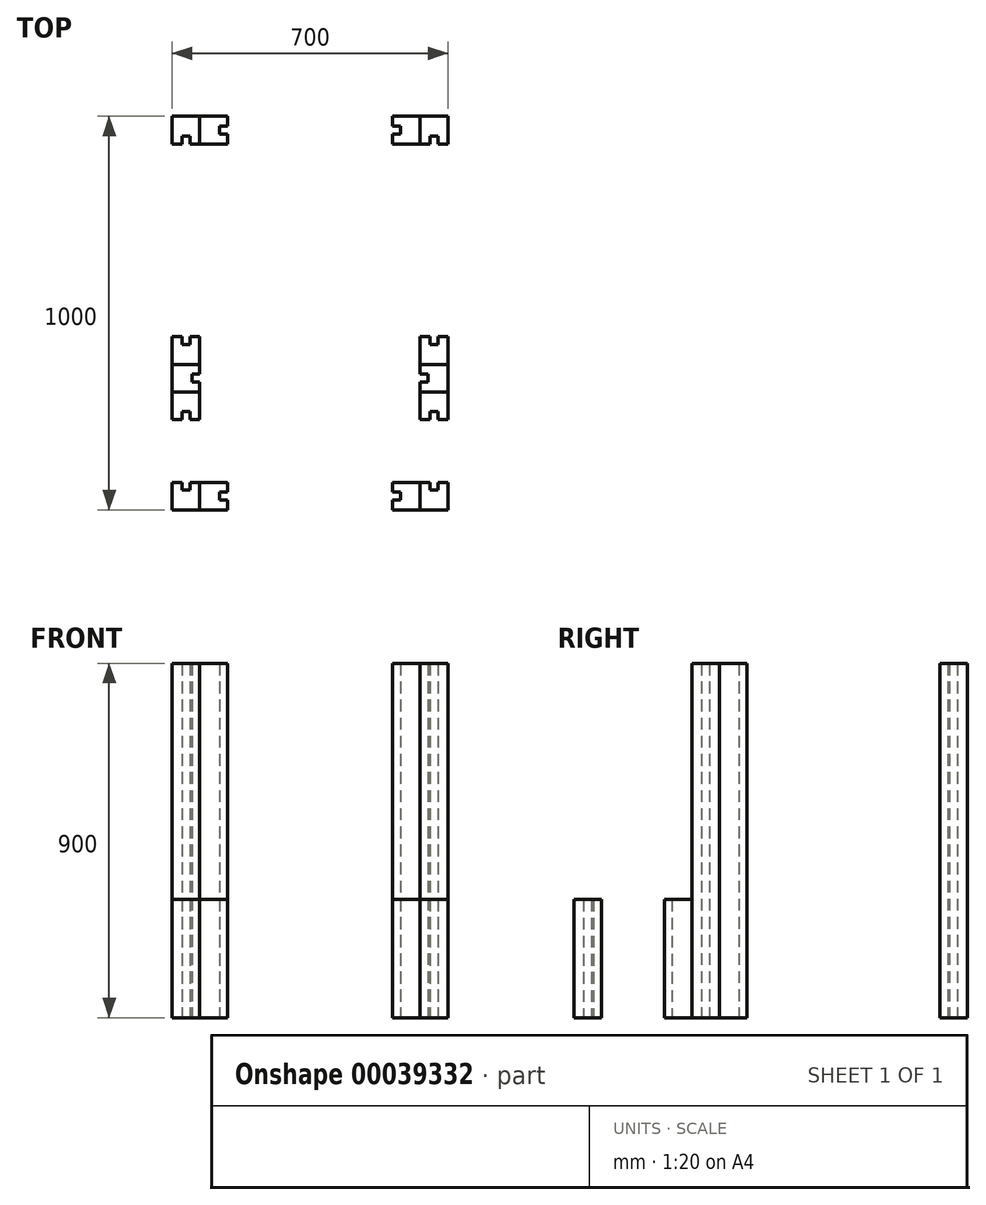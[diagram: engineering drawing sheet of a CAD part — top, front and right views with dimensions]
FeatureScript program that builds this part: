
annotation { "Feature Type Name" : "Feature", "Feature Type Description" : "" }
export const myFeature = defineFeature(function(context is Context, id is Id, definition is map)
    precondition{}
    {
        {
            var Q0;
            Q0=qCreatedBy(makeId("Top.planeOp"),FACE);
            var sketch = newSketch(context, id + "F0", { "sketchPlane" : qUnion([Q0])});
            skLineSegment(sketch, "E0", {"start": v(-350, 0) * mm, "end": v(-280, 0) * mm});
            skLineSegment(sketch, "E1", {"start": v(-280, 0) * mm, "end": v(-280, -70) * mm});
            skLineSegment(sketch, "E2", {"start": v(-280, -70) * mm, "end": v(-305, -70) * mm});
            skLineSegment(sketch, "E3", {"start": v(-305, -70) * mm, "end": v(-305, -50) * mm});
            skLineSegment(sketch, "E4", {"start": v(-305, -50) * mm, "end": v(-325, -50) * mm});
            skLineSegment(sketch, "E5", {"start": v(-325, -50) * mm, "end": v(-325, -70) * mm});
            skLineSegment(sketch, "E6", {"start": v(-325, -70) * mm, "end": v(-350, -70) * mm});
            skLineSegment(sketch, "E7", {"start": v(-350, -70) * mm, "end": v(-350, 0) * mm});
            skLineSegment(sketch, "E8", {"start": v(-350, -630) * mm, "end": v(-325, -630) * mm});
            skLineSegment(sketch, "E9", {"start": v(-325, -630) * mm, "end": v(-325, -650) * mm});
            skLineSegment(sketch, "E10", {"start": v(-325, -650) * mm, "end": v(-305, -650) * mm});
            skLineSegment(sketch, "E11", {"start": v(-305, -650) * mm, "end": v(-305, -630) * mm});
            skLineSegment(sketch, "E12", {"start": v(-305, -630) * mm, "end": v(-280, -630) * mm});
            skLineSegment(sketch, "E13", {"start": v(-280, -630) * mm, "end": v(-280, -700) * mm});
            skLineSegment(sketch, "E14", {"start": v(-280, -700) * mm, "end": v(-350, -700) * mm});
            skLineSegment(sketch, "E15", {"start": v(-350, -700) * mm, "end": v(-350, -630) * mm});
            skLineSegment(sketch, "E16", {"start": v(-350, -700) * mm, "end": v(-350, -770) * mm});
            skLineSegment(sketch, "E17", {"start": v(-350, -770) * mm, "end": v(-325, -770) * mm});
            skLineSegment(sketch, "E18", {"start": v(-325, -770) * mm, "end": v(-325, -750) * mm});
            skLineSegment(sketch, "E19", {"start": v(-325, -750) * mm, "end": v(-305, -750) * mm});
            skLineSegment(sketch, "E20", {"start": v(-305, -750) * mm, "end": v(-305, -770) * mm});
            skLineSegment(sketch, "E21", {"start": v(-305, -770) * mm, "end": v(-280, -770) * mm});
            skLineSegment(sketch, "E22", {"start": v(-280, -770) * mm, "end": v(-280, -700) * mm});
            skLineSegment(sketch, "E23", {"start": v(-350, -930) * mm, "end": v(-325, -930) * mm});
            skLineSegment(sketch, "E24", {"start": v(-325, -930) * mm, "end": v(-325, -950) * mm});
            skLineSegment(sketch, "E25", {"start": v(-325, -950) * mm, "end": v(-305, -950) * mm});
            skLineSegment(sketch, "E26", {"start": v(-305, -950) * mm, "end": v(-305, -930) * mm});
            skLineSegment(sketch, "E27", {"start": v(-305, -930) * mm, "end": v(-280, -930) * mm});
            skLineSegment(sketch, "E28", {"start": v(-280, -930) * mm, "end": v(-280, -1000) * mm});
            skLineSegment(sketch, "E29", {"start": v(-280, -1000) * mm, "end": v(-350, -1000) * mm});
            skLineSegment(sketch, "E30", {"start": v(-350, -1000) * mm, "end": v(-350, -930) * mm});
            skLineSegment(sketch, "E31", {"start": v(-280, 0) * mm, "end": v(-210, 0) * mm});
            skLineSegment(sketch, "E32", {"start": v(-210, 0) * mm, "end": v(-210, -25) * mm});
            skLineSegment(sketch, "E33", {"start": v(-210, -25) * mm, "end": v(-230, -25) * mm});
            skLineSegment(sketch, "E34", {"start": v(-230, -25) * mm, "end": v(-230, -45) * mm});
            skLineSegment(sketch, "E35", {"start": v(-230, -45) * mm, "end": v(-210, -45) * mm});
            skLineSegment(sketch, "E36", {"start": v(-210, -45) * mm, "end": v(-210, -70) * mm});
            skLineSegment(sketch, "E37", {"start": v(-210, -70) * mm, "end": v(-280, -70) * mm});
            skLineSegment(sketch, "E38", {"start": v(-280, -630) * mm, "end": v(-210, -630) * mm});
            skLineSegment(sketch, "E39", {"start": v(-210, -630) * mm, "end": v(-210, -655) * mm});
            skLineSegment(sketch, "E40", {"start": v(-210, -655) * mm, "end": v(-230, -655) * mm});
            skLineSegment(sketch, "E41", {"start": v(-230, -655) * mm, "end": v(-230, -675) * mm});
            skLineSegment(sketch, "E42", {"start": v(-230, -675) * mm, "end": v(-210, -675) * mm});
            skLineSegment(sketch, "E43", {"start": v(-210, -675) * mm, "end": v(-210, -700) * mm});
            skLineSegment(sketch, "E44", {"start": v(-210, -700) * mm, "end": v(-280, -700) * mm});
            skLineSegment(sketch, "E45", {"start": v(-280, -930) * mm, "end": v(-210, -930) * mm});
            skLineSegment(sketch, "E46", {"start": v(-210, -930) * mm, "end": v(-210, -955) * mm});
            skLineSegment(sketch, "E47", {"start": v(-210, -955) * mm, "end": v(-230, -955) * mm});
            skLineSegment(sketch, "E48", {"start": v(-230, -955) * mm, "end": v(-230, -975) * mm});
            skLineSegment(sketch, "E49", {"start": v(-230, -975) * mm, "end": v(-210, -975) * mm});
            skLineSegment(sketch, "E50", {"start": v(-210, -975) * mm, "end": v(-210, -1000) * mm});
            skLineSegment(sketch, "E51", {"start": v(-210, -1000) * mm, "end": v(-280, -1000) * mm});
            skSolve(sketch);
        }
        {
            var Q0;
            Q0=makeQuery(id+"F0.imprint","IMPRINT",FACE,{"disambiguationData":[TD([[makeQuery(id+"F0.imprint","IMPRINT",EDGE,{"derivedFrom":sQuery(id+"F0.wireOp",EDGE,"E0")}),-1.0]])]});
            extrude(context, id + "F1", {"entities" : qUnion([Q0]), "depth" : 900 * mm});
        }
        {
            var Q0;
            Q0=makeQuery(id+"F0.imprint","IMPRINT",FACE,{"disambiguationData":[TD([[makeQuery(id+"F0.imprint","IMPRINT",EDGE,{"derivedFrom":sQuery(id+"F0.wireOp",EDGE,"E1")}),1.0]])]});
            var Q1;
            Q1=makeQuery(id+"F1.opExtrude","CAP_FACE",FACE,{"disambiguationData":[OSD([sQuery(id+"F0.wireOp",EDGE,"E0"),sQuery(id+"F0.wireOp",EDGE,"E1"),sQuery(id+"F0.wireOp",EDGE,"E2"),sQuery(id+"F0.wireOp",EDGE,"E3"),sQuery(id+"F0.wireOp",EDGE,"E4"),sQuery(id+"F0.wireOp",EDGE,"E5"),sQuery(id+"F0.wireOp",EDGE,"E6"),sQuery(id+"F0.wireOp",EDGE,"E7")])],"isStart":false});
            extrude(context, id + "F2", {"entities" : qUnion([Q0]), "endBound" : BoundingType.UP_TO_SURFACE, "endBoundEntityFace" : qUnion([Q1]), "depth" : 25 * mm});
        }
        {
            var Q0;
            Q0=makeQuery(id+"F0.imprint","IMPRINT",FACE,{"disambiguationData":[TD([[makeQuery(id+"F0.imprint","IMPRINT",EDGE,{"derivedFrom":sQuery(id+"F0.wireOp",EDGE,"E8")}),-1.0]])]});
            var Q1;
            Q1=makeQuery(id+"F1.opExtrude","CAP_FACE",FACE,{"disambiguationData":[OSD([sQuery(id+"F0.wireOp",EDGE,"E0"),sQuery(id+"F0.wireOp",EDGE,"E1"),sQuery(id+"F0.wireOp",EDGE,"E2"),sQuery(id+"F0.wireOp",EDGE,"E3"),sQuery(id+"F0.wireOp",EDGE,"E4"),sQuery(id+"F0.wireOp",EDGE,"E5"),sQuery(id+"F0.wireOp",EDGE,"E6"),sQuery(id+"F0.wireOp",EDGE,"E7")])],"isStart":false});
            extrude(context, id + "F3", {"entities" : qUnion([Q0]), "endBound" : BoundingType.UP_TO_SURFACE, "endBoundEntityFace" : qUnion([Q1]), "depth" : 25 * mm});
        }
        {
            var Q0;
            Q0=makeQuery(id+"F0.imprint","IMPRINT",FACE,{"disambiguationData":[TD([[makeQuery(id+"F0.imprint","IMPRINT",EDGE,{"derivedFrom":sQuery(id+"F0.wireOp",EDGE,"E13")}),1.0]])]});
            var Q1;
            Q1=makeQuery(id+"F1.opExtrude","CAP_FACE",FACE,{"disambiguationData":[OSD([sQuery(id+"F0.wireOp",EDGE,"E0"),sQuery(id+"F0.wireOp",EDGE,"E1"),sQuery(id+"F0.wireOp",EDGE,"E2"),sQuery(id+"F0.wireOp",EDGE,"E3"),sQuery(id+"F0.wireOp",EDGE,"E4"),sQuery(id+"F0.wireOp",EDGE,"E5"),sQuery(id+"F0.wireOp",EDGE,"E6"),sQuery(id+"F0.wireOp",EDGE,"E7")])],"isStart":false});
            extrude(context, id + "F4", {"entities" : qUnion([Q0]), "endBound" : BoundingType.UP_TO_SURFACE, "endBoundEntityFace" : qUnion([Q1]), "depth" : 25 * mm});
        }
        {
            var Q0;
            Q0=makeQuery(id+"F0.imprint","IMPRINT",FACE,{"disambiguationData":[TD([[makeQuery(id+"F0.imprint","IMPRINT",EDGE,{"derivedFrom":sQuery(id+"F0.wireOp",EDGE,"E14")}),1.0]])]});
            extrude(context, id + "F5", {"entities" : qUnion([Q0]), "depth" : 300 * mm});
        }
        {
            var Q0;
            Q0=makeQuery(id+"F0.imprint","IMPRINT",FACE,{"disambiguationData":[TD([[makeQuery(id+"F0.imprint","IMPRINT",EDGE,{"derivedFrom":sQuery(id+"F0.wireOp",EDGE,"E23")}),-1.0]])]});
            var Q1;
            Q1=makeQuery(id+"F5.opExtrude","CAP_FACE",FACE,{"disambiguationData":[OSD([sQuery(id+"F0.wireOp",EDGE,"E14"),sQuery(id+"F0.wireOp",EDGE,"E16"),sQuery(id+"F0.wireOp",EDGE,"E17"),sQuery(id+"F0.wireOp",EDGE,"E18"),sQuery(id+"F0.wireOp",EDGE,"E19"),sQuery(id+"F0.wireOp",EDGE,"E20"),sQuery(id+"F0.wireOp",EDGE,"E21"),sQuery(id+"F0.wireOp",EDGE,"E22")])],"isStart":false});
            extrude(context, id + "F6", {"entities" : qUnion([Q0]), "endBound" : BoundingType.UP_TO_SURFACE, "endBoundEntityFace" : qUnion([Q1]), "depth" : 25 * mm});
        }
        {
            var Q0;
            Q0=makeQuery(id+"F0.imprint","IMPRINT",FACE,{"disambiguationData":[TD([[makeQuery(id+"F0.imprint","IMPRINT",EDGE,{"derivedFrom":sQuery(id+"F0.wireOp",EDGE,"E28")}),1.0]])]});
            var Q1;
            Q1=makeQuery(id+"F5.opExtrude","CAP_FACE",FACE,{"disambiguationData":[OSD([sQuery(id+"F0.wireOp",EDGE,"E14"),sQuery(id+"F0.wireOp",EDGE,"E16"),sQuery(id+"F0.wireOp",EDGE,"E17"),sQuery(id+"F0.wireOp",EDGE,"E18"),sQuery(id+"F0.wireOp",EDGE,"E19"),sQuery(id+"F0.wireOp",EDGE,"E20"),sQuery(id+"F0.wireOp",EDGE,"E21"),sQuery(id+"F0.wireOp",EDGE,"E22")])],"isStart":false});
            extrude(context, id + "F7", {"entities" : qUnion([Q0]), "endBound" : BoundingType.UP_TO_SURFACE, "endBoundEntityFace" : qUnion([Q1]), "depth" : 25 * mm});
        }
        {
            var Q0;
            Q0=makeQuery(id+"F1.opExtrude","SWEPT_BODY",BODY,{"disambiguationData":[OSD([sQuery(id+"F0.wireOp",EDGE,"E0"),sQuery(id+"F0.wireOp",EDGE,"E1"),sQuery(id+"F0.wireOp",EDGE,"E2"),sQuery(id+"F0.wireOp",EDGE,"E3"),sQuery(id+"F0.wireOp",EDGE,"E4"),sQuery(id+"F0.wireOp",EDGE,"E5"),sQuery(id+"F0.wireOp",EDGE,"E6"),sQuery(id+"F0.wireOp",EDGE,"E7")])]});
            var Q1;
            Q1=makeQuery(id+"F2.opExtrude","SWEPT_BODY",BODY,{"disambiguationData":[OSD([sQuery(id+"F0.wireOp",EDGE,"E1"),sQuery(id+"F0.wireOp",EDGE,"E31"),sQuery(id+"F0.wireOp",EDGE,"E32"),sQuery(id+"F0.wireOp",EDGE,"E33"),sQuery(id+"F0.wireOp",EDGE,"E34"),sQuery(id+"F0.wireOp",EDGE,"E35"),sQuery(id+"F0.wireOp",EDGE,"E36"),sQuery(id+"F0.wireOp",EDGE,"E37")])]});
            var Q2;
            Q2=makeQuery(id+"F3.opExtrude","SWEPT_BODY",BODY,{"disambiguationData":[OSD([sQuery(id+"F0.wireOp",EDGE,"E8"),sQuery(id+"F0.wireOp",EDGE,"E9"),sQuery(id+"F0.wireOp",EDGE,"E10"),sQuery(id+"F0.wireOp",EDGE,"E11"),sQuery(id+"F0.wireOp",EDGE,"E12"),sQuery(id+"F0.wireOp",EDGE,"E13"),sQuery(id+"F0.wireOp",EDGE,"E14"),sQuery(id+"F0.wireOp",EDGE,"E15")])]});
            var Q3;
            Q3=makeQuery(id+"F4.opExtrude","SWEPT_BODY",BODY,{"disambiguationData":[OSD([sQuery(id+"F0.wireOp",EDGE,"E13"),sQuery(id+"F0.wireOp",EDGE,"E38"),sQuery(id+"F0.wireOp",EDGE,"E39"),sQuery(id+"F0.wireOp",EDGE,"E40"),sQuery(id+"F0.wireOp",EDGE,"E41"),sQuery(id+"F0.wireOp",EDGE,"E42"),sQuery(id+"F0.wireOp",EDGE,"E43"),sQuery(id+"F0.wireOp",EDGE,"E44")])]});
            var Q4;
            Q4=makeQuery(id+"F5.opExtrude","SWEPT_BODY",BODY,{"disambiguationData":[OSD([sQuery(id+"F0.wireOp",EDGE,"E14"),sQuery(id+"F0.wireOp",EDGE,"E16"),sQuery(id+"F0.wireOp",EDGE,"E17"),sQuery(id+"F0.wireOp",EDGE,"E18"),sQuery(id+"F0.wireOp",EDGE,"E19"),sQuery(id+"F0.wireOp",EDGE,"E20"),sQuery(id+"F0.wireOp",EDGE,"E21"),sQuery(id+"F0.wireOp",EDGE,"E22")])]});
            var Q5;
            Q5=makeQuery(id+"F6.opExtrude","SWEPT_BODY",BODY,{"disambiguationData":[OSD([sQuery(id+"F0.wireOp",EDGE,"E23"),sQuery(id+"F0.wireOp",EDGE,"E24"),sQuery(id+"F0.wireOp",EDGE,"E25"),sQuery(id+"F0.wireOp",EDGE,"E26"),sQuery(id+"F0.wireOp",EDGE,"E27"),sQuery(id+"F0.wireOp",EDGE,"E28"),sQuery(id+"F0.wireOp",EDGE,"E29"),sQuery(id+"F0.wireOp",EDGE,"E30")])]});
            var Q6;
            Q6=makeQuery(id+"F7.opExtrude","SWEPT_BODY",BODY,{"disambiguationData":[OSD([sQuery(id+"F0.wireOp",EDGE,"E28"),sQuery(id+"F0.wireOp",EDGE,"E45"),sQuery(id+"F0.wireOp",EDGE,"E46"),sQuery(id+"F0.wireOp",EDGE,"E47"),sQuery(id+"F0.wireOp",EDGE,"E48"),sQuery(id+"F0.wireOp",EDGE,"E49"),sQuery(id+"F0.wireOp",EDGE,"E50"),sQuery(id+"F0.wireOp",EDGE,"E51")])]});
            var Q7;
            Q7=qCreatedBy(makeId("Right.planeOp"),FACE);
            mirror(context, id + "F8", {"entities" : qUnion([Q0, Q1, Q2, Q3, Q4, Q5, Q6]), "mirrorPlane" : qUnion([Q7])});
        }
        {
            var Q0;
            Q0=makeQuery(id+"F3.opExtrude","SWEPT_BODY",BODY,{"disambiguationData":[OSD([sQuery(id+"F0.wireOp",EDGE,"E8"),sQuery(id+"F0.wireOp",EDGE,"E9"),sQuery(id+"F0.wireOp",EDGE,"E10"),sQuery(id+"F0.wireOp",EDGE,"E11"),sQuery(id+"F0.wireOp",EDGE,"E12"),sQuery(id+"F0.wireOp",EDGE,"E13"),sQuery(id+"F0.wireOp",EDGE,"E14"),sQuery(id+"F0.wireOp",EDGE,"E15")])]});
            var Q1;
            Q1=makeQuery(id+"F8.opPattern","COPY",BODY,{"derivedFrom":makeQuery(id+"F3.opExtrude","SWEPT_BODY",BODY,{"disambiguationData":[OSD([sQuery(id+"F0.wireOp",EDGE,"E8"),sQuery(id+"F0.wireOp",EDGE,"E9"),sQuery(id+"F0.wireOp",EDGE,"E10"),sQuery(id+"F0.wireOp",EDGE,"E11"),sQuery(id+"F0.wireOp",EDGE,"E12"),sQuery(id+"F0.wireOp",EDGE,"E13"),sQuery(id+"F0.wireOp",EDGE,"E14"),sQuery(id+"F0.wireOp",EDGE,"E15")])]}),"instanceName":"1"});
            var Q2;
            Q2=makeQuery(id+"F3.opExtrude","CAP_VERTEX",VERTEX,{"disambiguationData":[OSD([sQuery(id+"F0.wireOp",EDGE,"E13"),sQuery(id+"F0.wireOp",EDGE,"E14"),sQuery(id+"F0.wireOp",EDGE,"E22"),sQuery(id+"F0.wireOp",EDGE,"E44")])],"isStart":false});
            var Q3;
            Q3=makeQuery(id+"F3.opExtrude","CAP_VERTEX",VERTEX,{"disambiguationData":[OSD([sQuery(id+"F0.wireOp",EDGE,"E12"),sQuery(id+"F0.wireOp",EDGE,"E13"),sQuery(id+"F0.wireOp",EDGE,"E38")])],"isStart":false});
            transform(context, id + "F9", {"entities" : qUnion([Q0, Q1]), "transformType" : TransformType.TRANSLATION_ENTITY, "oppositeDirectionEntity" : false, "transformLine" : qUnion([Q2, Q3]), "makeCopy" : false});
        }
        {
            var Q0;
            Q0=makeQuery(id+"F4.opExtrude","SWEPT_BODY",BODY,{"disambiguationData":[OSD([sQuery(id+"F0.wireOp",EDGE,"E13"),sQuery(id+"F0.wireOp",EDGE,"E38"),sQuery(id+"F0.wireOp",EDGE,"E39"),sQuery(id+"F0.wireOp",EDGE,"E40"),sQuery(id+"F0.wireOp",EDGE,"E41"),sQuery(id+"F0.wireOp",EDGE,"E42"),sQuery(id+"F0.wireOp",EDGE,"E43"),sQuery(id+"F0.wireOp",EDGE,"E44")])]});
            var Q1;
            Q1=makeQuery(id+"F3.opExtrude","CAP_VERTEX",VERTEX,{"disambiguationData":[OSD([sQuery(id+"F0.wireOp",EDGE,"E13"),sQuery(id+"F0.wireOp",EDGE,"E14"),sQuery(id+"F0.wireOp",EDGE,"E22"),sQuery(id+"F0.wireOp",EDGE,"E44")])],"isStart":false});
            var Q2;
            Q2=makeQuery(id+"F3.opExtrude","CAP_VERTEX",VERTEX,{"disambiguationData":[OSD([sQuery(id+"F0.wireOp",EDGE,"E14"),sQuery(id+"F0.wireOp",EDGE,"E15"),sQuery(id+"F0.wireOp",EDGE,"E16")])],"isStart":false});
            transform(context, id + "F10", {"entities" : qUnion([Q0]), "transformType" : TransformType.TRANSLATION_ENTITY, "oppositeDirectionEntity" : false, "transformLine" : qUnion([Q1, Q2]), "makeCopy" : false});
        }
        {
            var Q0;
            Q0=makeQuery(id+"F8.opPattern","COPY",BODY,{"derivedFrom":makeQuery(id+"F4.opExtrude","SWEPT_BODY",BODY,{"disambiguationData":[OSD([sQuery(id+"F0.wireOp",EDGE,"E13"),sQuery(id+"F0.wireOp",EDGE,"E38"),sQuery(id+"F0.wireOp",EDGE,"E39"),sQuery(id+"F0.wireOp",EDGE,"E40"),sQuery(id+"F0.wireOp",EDGE,"E41"),sQuery(id+"F0.wireOp",EDGE,"E42"),sQuery(id+"F0.wireOp",EDGE,"E43"),sQuery(id+"F0.wireOp",EDGE,"E44")])]}),"instanceName":"1"});
            var Q1;
            Q1=makeQuery(id+"F8.opPattern","COPY",VERTEX,{"derivedFrom":makeQuery(id+"F3.opExtrude","CAP_VERTEX",VERTEX,{"disambiguationData":[OSD([sQuery(id+"F0.wireOp",EDGE,"E13"),sQuery(id+"F0.wireOp",EDGE,"E14"),sQuery(id+"F0.wireOp",EDGE,"E22"),sQuery(id+"F0.wireOp",EDGE,"E44")])],"isStart":false}),"instanceName":"1"});
            var Q2;
            Q2=makeQuery(id+"F8.opPattern","COPY",VERTEX,{"derivedFrom":makeQuery(id+"F3.opExtrude","CAP_VERTEX",VERTEX,{"disambiguationData":[OSD([sQuery(id+"F0.wireOp",EDGE,"E14"),sQuery(id+"F0.wireOp",EDGE,"E15"),sQuery(id+"F0.wireOp",EDGE,"E16")])],"isStart":false}),"instanceName":"1"});
            transform(context, id + "F11", {"entities" : qUnion([Q0]), "transformType" : TransformType.TRANSLATION_ENTITY, "oppositeDirectionEntity" : false, "transformLine" : qUnion([Q1, Q2]), "makeCopy" : false});
        }
    });
